# Revit family: Bath-Drop_In-Whirlpool-Heater-KOHLER-Underscore-K-1835_1
name_source: partatom
category: Plumbing Fixtures
units: mm (PartAtom-declared; Revit-internal decimal feet)

## family parameters
Cut with Voids When Loaded = No
Host = Face
OmniClass Number = 23.31.15.00
OmniClass Title = Bathtubs
Part Type = Normal
Room Calculation Point = No
Round Connector Dimension = Use Diameter
Shared = No

## types (1)
- 0-White
    ADA Compliant = No
    Amplifer Electrical Connector = Amplifer Electrical Connector
    Apparent Load = 1800 VA
    Assembly Code = D2010500
    Blower Electrical Connector = Blower Electrical Connector
    CW Connection = No
    Cold Water Inlet = Cold Water Inlet
    Date Modified = 06/30/2023
    Default Elevation = 0"
    Description = 72 inch x 36 inch drop-in heated whirlpool bath
    Drain Included = No
    Electrical Connector = Yes
    Electrical Note = Three dedicated circuits required, protected with Class A Ground-Fault Circuit-Interrupter (GFCI). Outside North America,
this device may be known as a Residual Current Device (RCD)
    Finish = KOHLER-Acrylic-0-White
    HW Connection = No
    Heater Electrical Connector = Heater Electrical Connector
    Height = 23 1/4"
    Hot Water Inlet = Hot Water Inlet
    Length = 72 3/16"
    Manufacturer = Kohler Co.
    Master Format 2014 = 22 41 19
    Master Format 2014 Name = Residential Bathtubs
    Material = Acylic
    Model = K-1835-JH-0
    Product Documentation Link = https://www.us.kohler.com
    Product Name = Underscore
    Product Page URL = http://www.us.kohler.com
    Pump Electrical Connector = Pump Electrical Connector
    Type = 1
    URL = https://www.us.kohler.com
    Vent Connection = No
    Voltage = 120 V
    Waste Connection = Yes
    Waste Water Outlet = Waste Water Outlet
    WaterSense Certified = No
    Width = 36"

## geometry (parser evidence)
native form markers: Sweep x5
no freeform markers — native parametric forms only
